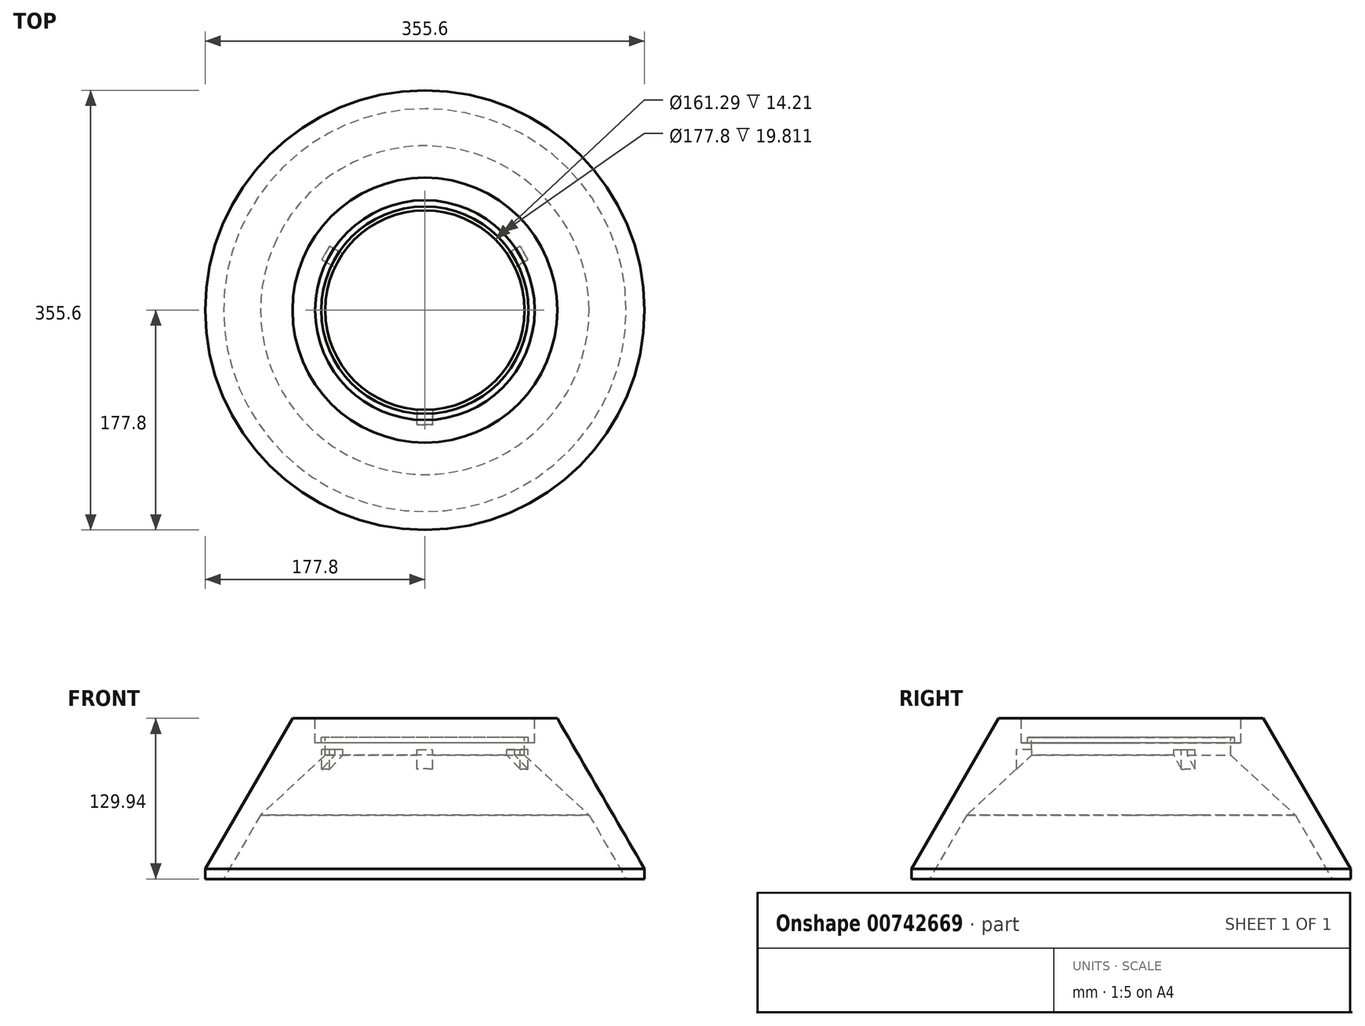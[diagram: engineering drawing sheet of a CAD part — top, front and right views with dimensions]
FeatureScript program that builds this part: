
annotation { "Feature Type Name" : "Feature", "Feature Type Description" : "" }
export const myFeature = defineFeature(function(context is Context, id is Id, definition is map)
    precondition{}
    {
        {
            var Q0;
            Q0=qCreatedBy(makeId("Front.planeOp"),FACE);
            var sketch = newSketch(context, id + "F0", { "sketchPlane" : qUnion([Q0])});
            skLineSegment(sketch, "E0", {"start": v(0, 62.29) * mm, "end": v(0, -74.77) * mm, "construction": true});
            skLineSegment(sketch, "E1", {"start": v(-83.82, 14.48) * mm, "end": v(-88.9, 14.48) * mm});
            skLineSegment(sketch, "E2", {"start": v(-88.9, 14.48) * mm, "end": v(-88.9, 34.3) * mm});
            skLineSegment(sketch, "E3", {"start": v(-88.9, 34.3) * mm, "end": v(-107.18, 34.3) * mm});
            skLineSegment(sketch, "E4", {"start": v(-107.18, 34.3) * mm, "end": v(-177.8, -87.4) * mm});
            skLineSegment(sketch, "E5", {"start": v(-177.8, -87.4) * mm, "end": v(-177.8, -95.65) * mm});
            skLineSegment(sketch, "E6", {"start": v(-177.8, -95.65) * mm, "end": v(-162.95, -95.65) * mm});
            skLineSegment(sketch, "E7", {"start": v(-162.95, -95.65) * mm, "end": v(-133.01, -44.05) * mm});
            skLineSegment(sketch, "E8", {"start": v(-133.01, -44.05) * mm, "end": v(-80.64, 4.53) * mm});
            skLineSegment(sketch, "E9", {"start": v(-83.82, 14.48) * mm, "end": v(-83.82, 18.75) * mm});
            skLineSegment(sketch, "E10", {"start": v(-83.82, 18.75) * mm, "end": v(-80.64, 18.75) * mm});
            skLineSegment(sketch, "E11", {"start": v(-80.64, 18.75) * mm, "end": v(-80.64, 4.53) * mm});
            skLineSegment(sketch, "E12", {"start": v(-133.99, -65.17) * mm, "end": v(-133.99, -95.65) * mm, "construction": true});
            skPoint(sketch, "E13", {"position": v(0, 0) * mm});
            skLineSegment(sketch, "E14", {"start": v(-49.74, 8.9) * mm, "end": v(-104.02, 8.9) * mm, "construction": true});
            skSolve(sketch);
        }
        {
            var Q0;
            Q0=makeQuery(id+"F0.imprint","IMPRINT",FACE,{"disambiguationData":[TD([[makeQuery(id+"F0.imprint","IMPRINT",EDGE,{"derivedFrom":sQuery(id+"F0.wireOp",EDGE,"E1")}),1.0]])]});
            var Q1;
            Q1=sQuery(id+"F0.wireOp",EDGE,"E0");
            revolve(context, id + "F1", {"surfaceOperationType" : NewSurfaceOperationType.NEW, "entities" : qUnion([Q0]), "axis" : qUnion([Q1]), "revolveType" : RevolveType.FULL});
        }
        {
            var Q0;
            Q0=makeQuery(id+"F1.opRevolve","SWEPT_FACE",FACE,{"disambiguationData":[OSD([sQuery(id+"F0.wireOp",EDGE,"E3")])]});
            cPlane(context, id + "F2", {"entities" : qUnion([Q0]), "cplaneType" : CPlaneType.OFFSET, "offset" : 25.4 * mm, "oppositeDirection" : true, "width" : 152.4 * mm, "height" : 152.4 * mm});
        }
        {
            var Q0;
            Q0=qCreatedBy(id+"F2.planeOp",FACE);
            var sketch = newSketch(context, id + "F3", { "sketchPlane" : qUnion([Q0])});
            skLineSegment(sketch, "E15", {"start": v(0, 0) * mm, "end": v(0, -86.36) * mm, "construction": true});
            skLineSegment(sketch, "E16.bottom", {"start": v(6.35, -66.04) * mm, "end": v(-6.35, -66.04) * mm});
            skLineSegment(sketch, "E16.left", {"start": v(6.35, -66.04) * mm, "end": v(6.35, -86.36) * mm});
            skLineSegment(sketch, "E16.right", {"start": v(-6.35, -66.04) * mm, "end": v(-6.35, -86.36) * mm});
            skPoint(sketch, "E16.middle", {"position": v(0, -76.2) * mm});
            skPoint(sketch, "E17.center", {"position": v(0, 0) * mm});
            skLineSegment(sketch, "E17.anchor2", {"start": v(0, 0) * mm, "end": v(74.79, 43.18) * mm, "construction": true});
            skLineSegment(sketch, "E18", {"start": v(-6.35, -86.36) * mm, "end": v(-6.35, -92.7) * mm});
            skPoint(sketch, "E18.endSnap0", {"position": v(0, -92.7) * mm});
            skLineSegment(sketch, "E19", {"start": v(-6.35, -92.7) * mm, "end": v(6.35, -92.71) * mm});
            skLineSegment(sketch, "E20", {"start": v(6.35, -92.71) * mm, "end": v(6.35, -86.36) * mm});
            skLineSegment(sketch, "E21.trimOffspring", {"start": v(0, -92.7) * mm, "end": v(0, -97.07) * mm, "construction": true});
            skLineSegment(sketch, "E22.1.0", {"start": v(-71.61, 48.68) * mm, "end": v(-77.11, 51.85) * mm});
            skPoint(sketch, "E22.1.1", {"position": v(-80.29, 46.35) * mm});
            skLineSegment(sketch, "E22.1.2", {"start": v(-54.02, 38.52) * mm, "end": v(-71.61, 48.68) * mm});
            skPoint(sketch, "E22.1.3", {"position": v(-66, 38.1) * mm});
            skLineSegment(sketch, "E22.1.4", {"start": v(-83.46, 40.86) * mm, "end": v(-77.96, 37.68) * mm});
            skLineSegment(sketch, "E22.1.5", {"start": v(-60.37, 27.52) * mm, "end": v(-77.96, 37.68) * mm});
            skLineSegment(sketch, "E22.1.6", {"start": v(-60.37, 27.52) * mm, "end": v(-54.02, 38.52) * mm});
            skLineSegment(sketch, "E22.1.7", {"start": v(-80.29, 46.35) * mm, "end": v(-84.06, 48.53) * mm, "construction": true});
            skLineSegment(sketch, "E22.1.8", {"start": v(-77.11, 51.85) * mm, "end": v(-83.46, 40.86) * mm});
            skLineSegment(sketch, "E22.2.0", {"start": v(77.96, 37.68) * mm, "end": v(83.46, 40.86) * mm});
            skPoint(sketch, "E22.2.1", {"position": v(80.29, 46.36) * mm});
            skLineSegment(sketch, "E22.2.2", {"start": v(60.37, 27.52) * mm, "end": v(77.96, 37.68) * mm});
            skPoint(sketch, "E22.2.3", {"position": v(66, 38.1) * mm});
            skLineSegment(sketch, "E22.2.4", {"start": v(77.11, 51.85) * mm, "end": v(71.61, 48.68) * mm});
            skLineSegment(sketch, "E22.2.5", {"start": v(54.02, 38.52) * mm, "end": v(71.61, 48.68) * mm});
            skLineSegment(sketch, "E22.2.6", {"start": v(54.02, 38.52) * mm, "end": v(60.37, 27.52) * mm});
            skLineSegment(sketch, "E22.2.7", {"start": v(80.29, 46.35) * mm, "end": v(84.06, 48.53) * mm, "construction": true});
            skLineSegment(sketch, "E22.2.8", {"start": v(83.46, 40.86) * mm, "end": v(77.11, 51.85) * mm});
            skLineSegment(sketch, "E22.anchor1", {"start": v(0, 0) * mm, "end": v(0, -92.7) * mm, "construction": true});
            skLineSegment(sketch, "E22.anchor2", {"start": v(0, 0) * mm, "end": v(80.29, 46.36) * mm, "construction": true});
            skPoint(sketch, "E23", {"position": v(-6.35, -77.3) * mm});
            skSolve(sketch);
        }
        {
            var Q0;
            Q0=qSketchRegion(id+"F3",true);
            extrude(context, id + "F4", {"entities" : qUnion([Q0]), "operationType" : NewBodyOperationType.REMOVE, "oppositeDirection" : true, "depth" : 25.4 * mm, "offsetDistance" : 25.4 * mm});
        }
    });
